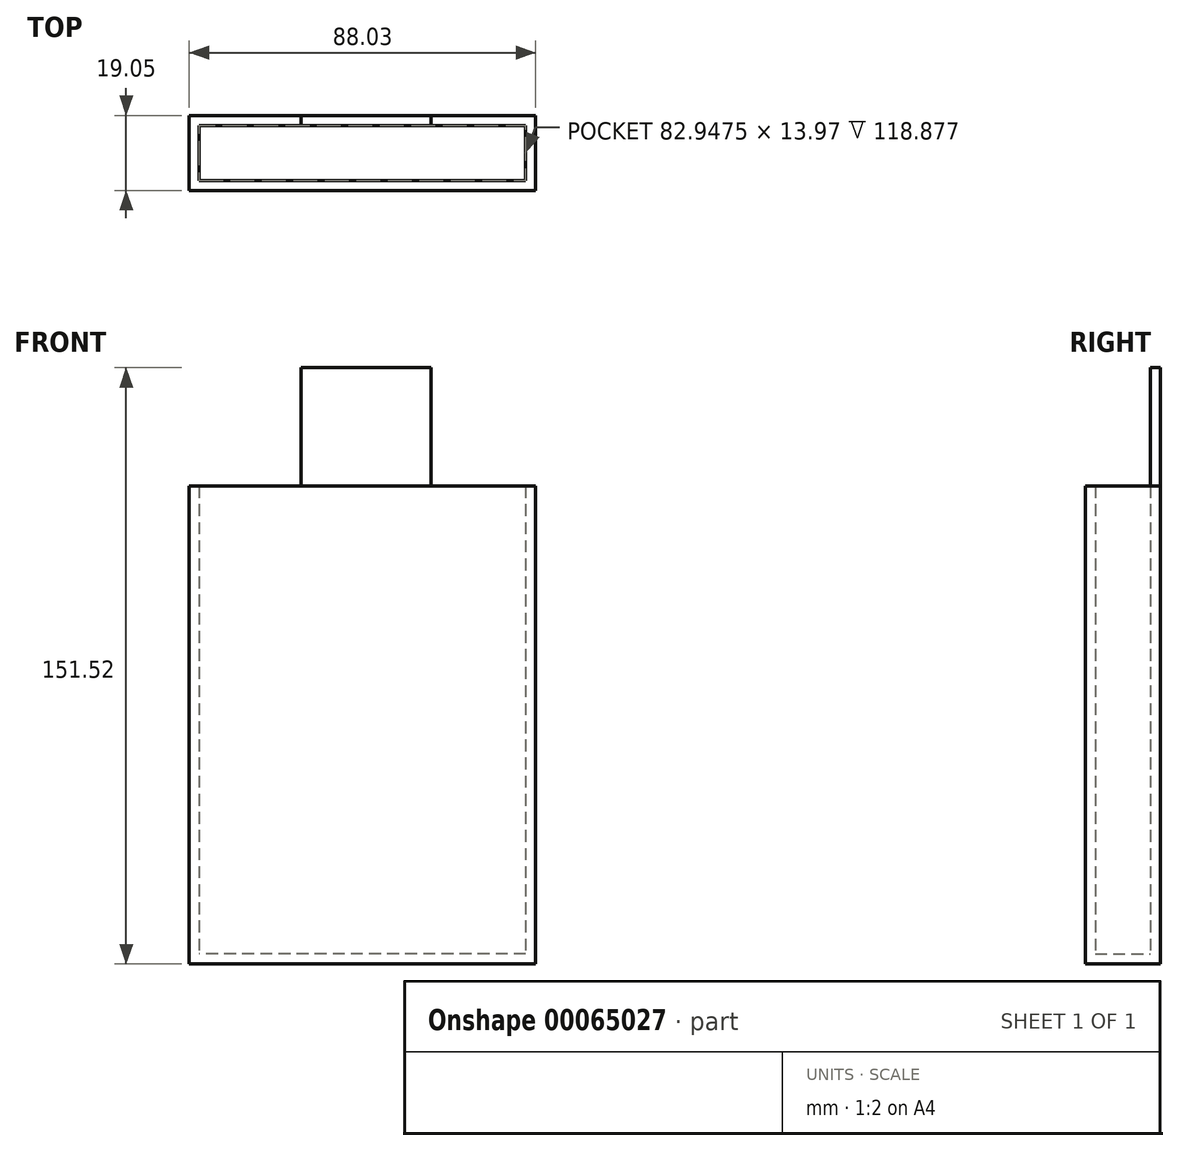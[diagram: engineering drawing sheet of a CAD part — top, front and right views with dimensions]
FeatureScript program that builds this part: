
annotation { "Feature Type Name" : "Feature", "Feature Type Description" : "" }
export const myFeature = defineFeature(function(context is Context, id is Id, definition is map)
    precondition{}
    {
        {
            var Q0;
            Q0=qCreatedBy(makeId("Front.planeOp"),FACE);
            var sketch = newSketch(context, id + "F0", { "sketchPlane" : qUnion([Q0])});
            skPoint(sketch, "E0.rect.middle", {"position": v(0, 0) * mm});
            skLineSegment(sketch, "E1.bottom", {"start": v(41.74, 60.85) * mm, "end": v(-46.3, 60.85) * mm});
            skLineSegment(sketch, "E1.top", {"start": v(41.74, -60.57) * mm, "end": v(-46.3, -60.57) * mm});
            skLineSegment(sketch, "E1.left", {"start": v(41.74, 60.85) * mm, "end": v(41.74, -60.57) * mm});
            skLineSegment(sketch, "E1.right", {"start": v(-46.3, 60.85) * mm, "end": v(-46.3, -60.57) * mm});
            skSolve(sketch);
        }
        {
            var Q0;
            Q0 = qSketchRegion(id + "F0", true);
            extrude(context, id + "F1", {"entities" : qUnion([Q0]), "depth" : 19.05 * mm});
        }
        {
            var Q0;
            Q0=makeQuery(id+"F1.opExtrude","SWEPT_FACE",FACE,{"disambiguationData":[OSD([sQuery(id+"F0.wireOp",EDGE,"E1.bottom")])]});
            shell(context, id + "F2", {"entities" : qUnion([Q0]), "thickness" : 2.54 * mm});
        }
        {
            var Q0;
            Q0=makeQuery(id+"F0.imprint","IMPRINT",FACE,{"disambiguationData":[TD([[makeQuery(id+"F0.imprint","IMPRINT",EDGE,{"derivedFrom":sQuery(id+"F0.wireOp",EDGE,"E1.bottom")}),1.0]])]});
            var sketch = newSketch(context, id + "F3", { "sketchPlane" : qUnion([Q0])});
            skLineSegment(sketch, "E2.bottom", {"start": v(15.18, 90.95) * mm, "end": v(-17.82, 90.95) * mm});
            skLineSegment(sketch, "E2.top", {"start": v(15.18, 59.55) * mm, "end": v(-17.82, 59.55) * mm});
            skLineSegment(sketch, "E2.left", {"start": v(15.18, 90.95) * mm, "end": v(15.18, 59.55) * mm});
            skLineSegment(sketch, "E2.right", {"start": v(-17.82, 90.95) * mm, "end": v(-17.82, 59.55) * mm});
            skSolve(sketch);
        }
        {
            var Q0;
            {var subQ0=sQuery(id+"F3.wireOp",EDGE,"E2.bottom");Q0=makeQuery(id+"F3.imprint","IMPRINT",FACE,{"disambiguationData":[TD([[makeQuery(id+"F3.imprint","IMPRINT",EDGE,{"derivedFrom":subQ0}),1.0]])]});}
            extrude(context, id + "F4", {"entities" : qUnion([Q0]), "operationType" : NewBodyOperationType.ADD, "depth" : 2.54 * mm});
        }
    });
